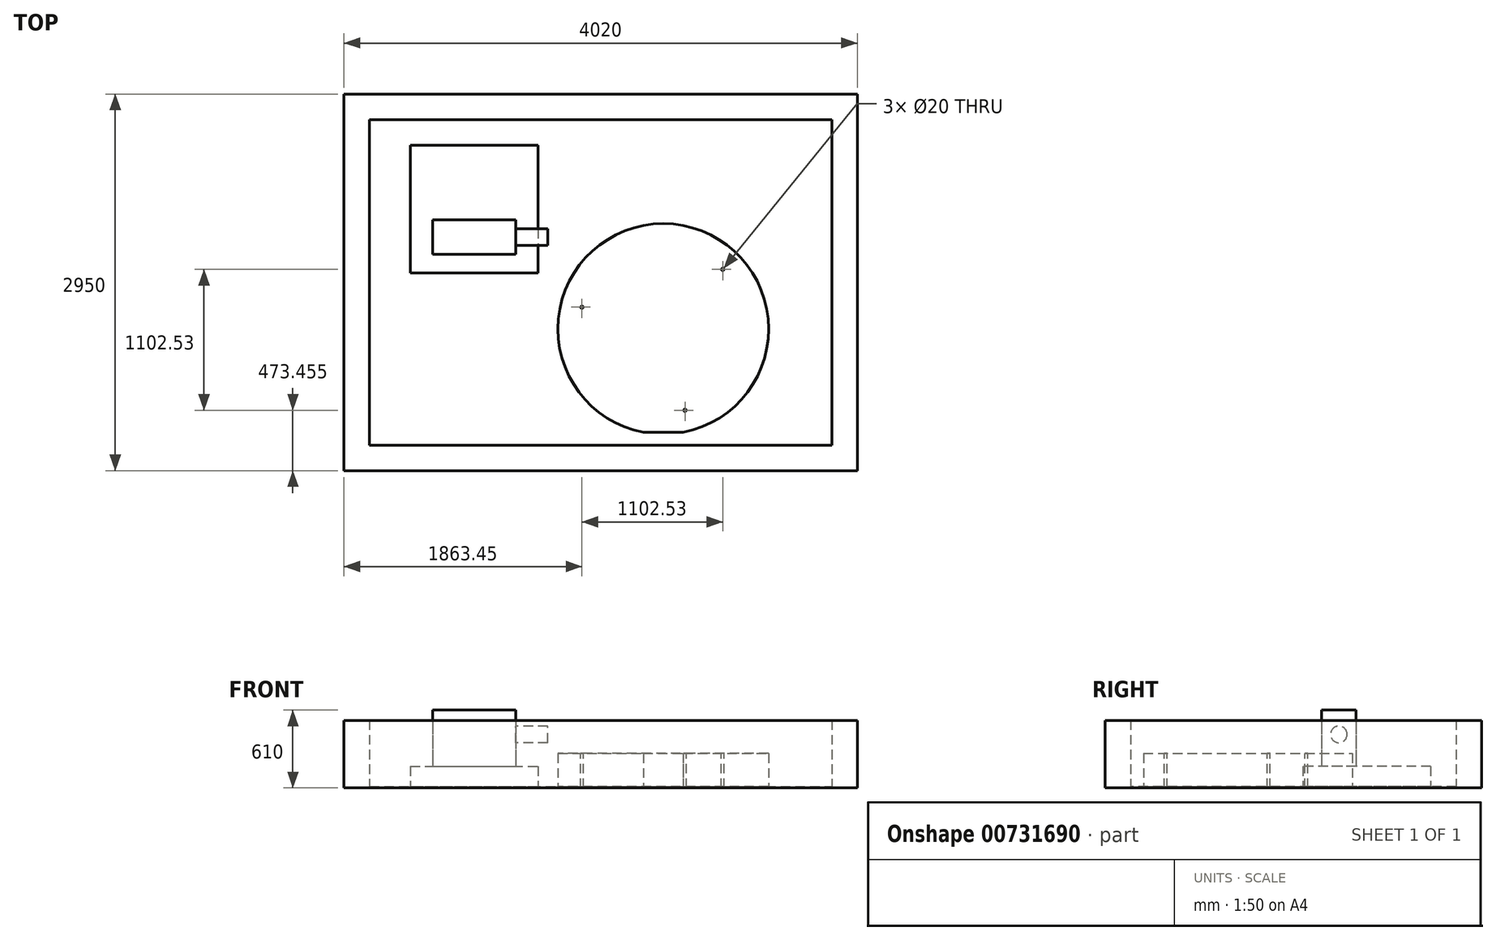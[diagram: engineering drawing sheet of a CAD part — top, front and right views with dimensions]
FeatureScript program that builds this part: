
annotation { "Feature Type Name" : "Feature", "Feature Type Description" : "" }
export const myFeature = defineFeature(function(context is Context, id is Id, definition is map)
    precondition{}
    {
        {
            var Q0;
            Q0=qCreatedBy(makeId("Top.planeOp"),FACE);
            var sketch = newSketch(context, id + "F0", { "sketchPlane" : qUnion([Q0])});
            skLineSegment(sketch, "E0.bottom", {"start": v(-2010, 1475) * mm, "end": v(2010, 1475) * mm});
            skLineSegment(sketch, "E0.top", {"start": v(-2010, -1475) * mm, "end": v(2010, -1475) * mm});
            skLineSegment(sketch, "E0.left", {"start": v(-2010, 1475) * mm, "end": v(-2010, -1475) * mm});
            skLineSegment(sketch, "E0.right", {"start": v(2010, 1475) * mm, "end": v(2010, -1475) * mm});
            skLineSegment(sketch, "E1", {"start": v(-2010, 1475) * mm, "end": v(2010, -1475) * mm, "construction": true});
            skSolve(sketch);
        }
        {
            var Q0;
            Q0=makeQuery(id+"F0.imprint","IMPRINT",FACE,{"disambiguationData":[TD([[makeQuery(id+"F0.imprint","IMPRINT",EDGE,{"derivedFrom":sQuery(id+"F0.wireOp",EDGE,"E0.bottom")}),-1.0]])]});
            extrude(context, id + "F1", {"entities" : qUnion([Q0]), "depth" : 10 * mm, "offsetDistance" : 25 * mm});
        }
        {
            var Q0;
            Q0=makeQuery(id+"F1.opExtrude","CAP_FACE",FACE,{"disambiguationData":[OSD([sQuery(id+"F0.wireOp",EDGE,"E0.bottom"),sQuery(id+"F0.wireOp",EDGE,"E0.top"),sQuery(id+"F0.wireOp",EDGE,"E0.left"),sQuery(id+"F0.wireOp",EDGE,"E0.right")])],"isStart":false});
            var sketch = newSketch(context, id + "F2", { "sketchPlane" : qUnion([Q0])});
            skLineSegment(sketch, "E2.bottom", {"start": v(-2010, 1475) * mm, "end": v(2010, 1475) * mm});
            skLineSegment(sketch, "E2.top", {"start": v(-2010, -1475) * mm, "end": v(2010, -1475) * mm});
            skLineSegment(sketch, "E2.left", {"start": v(-2010, 1475) * mm, "end": v(-2010, -1475) * mm});
            skLineSegment(sketch, "E2.right", {"start": v(2010, 1475) * mm, "end": v(2010, -1475) * mm});
            skLineSegment(sketch, "E3.bottom", {"start": v(-1810, 1275) * mm, "end": v(1810, 1275) * mm});
            skLineSegment(sketch, "E3.top", {"start": v(-1810, -1275) * mm, "end": v(1810, -1275) * mm});
            skLineSegment(sketch, "E3.left", {"start": v(-1810, 1275) * mm, "end": v(-1810, -1275) * mm});
            skLineSegment(sketch, "E3.right", {"start": v(1810, 1275) * mm, "end": v(1810, -1275) * mm});
            skSolve(sketch);
        }
        {
            var Q0;
            Q0 = qSketchRegion(id + "F2", true);
            extrude(context, id + "F3", {"entities" : qUnion([Q0]), "operationType" : NewBodyOperationType.ADD, "depth" : 520 * mm, "offsetDistance" : 25 * mm});
        }
        {
            var Q0;
            Q0=makeQuery(id+"F1.opExtrude","CAP_FACE",FACE,{"disambiguationData":[OSD([sQuery(id+"F0.wireOp",EDGE,"E0.bottom"),sQuery(id+"F0.wireOp",EDGE,"E0.top"),sQuery(id+"F0.wireOp",EDGE,"E0.left"),sQuery(id+"F0.wireOp",EDGE,"E0.right")])],"isStart":false});
            var sketch = newSketch(context, id + "F4", { "sketchPlane" : qUnion([Q0])});
            skLineSegment(sketch, "E4.bottom", {"start": v(-1490, 1075) * mm, "end": v(-490, 1075) * mm});
            skLineSegment(sketch, "E4.top", {"start": v(-1490, 75) * mm, "end": v(-490, 75) * mm});
            skLineSegment(sketch, "E4.left", {"start": v(-1490, 1075) * mm, "end": v(-1490, 75) * mm});
            skLineSegment(sketch, "E4.right", {"start": v(-490, 1075) * mm, "end": v(-490, 75) * mm});
            skSolve(sketch);
        }
        {
            var Q0;
            Q0 = qSketchRegion(id + "F4", true);
            extrude(context, id + "F5", {"entities" : qUnion([Q0]), "operationType" : NewBodyOperationType.ADD, "depth" : 160 * mm, "offsetDistance" : 25 * mm});
        }
        {
            var Q0;
            Q0=makeQuery(id+"F1.opExtrude","CAP_FACE",FACE,{"disambiguationData":[OSD([sQuery(id+"F0.wireOp",EDGE,"E0.bottom"),sQuery(id+"F0.wireOp",EDGE,"E0.top"),sQuery(id+"F0.wireOp",EDGE,"E0.left"),sQuery(id+"F0.wireOp",EDGE,"E0.right")])],"isStart":false});
            var sketch = newSketch(context, id + "F6", { "sketchPlane" : qUnion([Q0])});
            skArc(sketch, "E5", {"start": v(646.6, -1175) * mm, "mid": v(490, 460) * mm, "end": v(333.4, -1175) * mm});
            skLineSegment(sketch, "E6", {"start": v(333.4, -1175) * mm, "end": v(646.6, -1175) * mm});
            skCircle(sketch, "E7", {"center": v(490, -365) * mm, "radius": 659 * mm, "construction": true});
            skPoint(sketch, "E8", {"position": v(490, -1024) * mm});
            skLineSegment(sketch, "E9", {"start": v(490, -365) * mm, "end": v(660.56, -1001.55) * mm, "construction": true});
            skLineSegment(sketch, "E10", {"start": v(490, -365) * mm, "end": v(-146.55, -535.56) * mm, "construction": true});
            skLineSegment(sketch, "E11", {"start": v(490, -365) * mm, "end": v(955.98, 100.98) * mm, "construction": true});
            skSolve(sketch);
        }
        {
            var Q0;
            Q0 = qSketchRegion(id + "F6", true);
            extrude(context, id + "F7", {"entities" : qUnion([Q0]), "operationType" : NewBodyOperationType.ADD, "depth" : 260 * mm, "offsetDistance" : 25 * mm});
        }
        {
            var Q0;
            Q0=makeQuery(id+"F5.opExtrude","CAP_FACE",FACE,{"disambiguationData":[OSD([sQuery(id+"F4.wireOp",EDGE,"E4.bottom"),sQuery(id+"F4.wireOp",EDGE,"E4.top"),sQuery(id+"F4.wireOp",EDGE,"E4.left"),sQuery(id+"F4.wireOp",EDGE,"E4.right")])],"isStart":false});
            var sketch = newSketch(context, id + "F8", { "sketchPlane" : qUnion([Q0])});
            skLineSegment(sketch, "E12.bottom", {"start": v(-1315, 490) * mm, "end": v(-665, 490) * mm});
            skLineSegment(sketch, "E12.top", {"start": v(-1315, 220) * mm, "end": v(-665, 220) * mm});
            skLineSegment(sketch, "E12.left", {"start": v(-1315, 490) * mm, "end": v(-1315, 220) * mm});
            skLineSegment(sketch, "E12.right", {"start": v(-665, 490) * mm, "end": v(-665, 220) * mm});
            skLineSegment(sketch, "E13", {"start": v(-1315, 490) * mm, "end": v(-665, 220) * mm, "construction": true});
            skPoint(sketch, "E14", {"position": v(-990, 355) * mm});
            skSolve(sketch);
        }
        {
            var Q0;
            Q0 = qSketchRegion(id + "F8", true);
            extrude(context, id + "F9", {"entities" : qUnion([Q0]), "operationType" : NewBodyOperationType.ADD, "depth" : 440 * mm, "offsetDistance" : 25 * mm});
        }
        {
            var Q0;
            Q0=makeQuery(id+"F9.opExtrude","SWEPT_FACE",FACE,{"disambiguationData":[OSD([sQuery(id+"F8.wireOp",EDGE,"E12.right")])]});
            var sketch = newSketch(context, id + "F10", { "sketchPlane" : qUnion([Q0])});
            skCircle(sketch, "E15", {"center": v(355, 420) * mm, "radius": 65 * mm});
            skPoint(sketch, "E15.centerSnap0", {"position": v(355, 170) * mm});
            skSolve(sketch);
        }
        {
            var Q0;
            Q0 = qSketchRegion(id + "F10", true);
            extrude(context, id + "F11", {"entities" : qUnion([Q0]), "operationType" : NewBodyOperationType.ADD, "depth" : 250 * mm, "offsetDistance" : 25 * mm});
        }
        {
            var Q0;
            Q0=makeQuery(id+"F7.opExtrude","CAP_FACE",FACE,{"disambiguationData":[OSD([sQuery(id+"F6.wireOp",EDGE,"E5"),sQuery(id+"F6.wireOp",EDGE,"E6")])],"isStart":false});
            var sketch = newSketch(context, id + "F12", { "sketchPlane" : qUnion([Q0])});
            skCircle(sketch, "E16", {"center": v(490, -365) * mm, "radius": 659 * mm, "construction": true});
            skCircle(sketch, "E17", {"center": v(955.98, 100.98) * mm, "radius": 10 * mm});
            skCircle(sketch, "E18", {"center": v(660.56, -1001.55) * mm, "radius": 10 * mm});
            skCircle(sketch, "E19", {"center": v(-146.55, -194.44) * mm, "radius": 10 * mm});
            skLineSegment(sketch, "E20", {"start": v(490, -365) * mm, "end": v(-146.55, -194.44) * mm, "construction": true});
            skLineSegment(sketch, "E21", {"start": v(490, -365) * mm, "end": v(955.98, 100.98) * mm, "construction": true});
            skLineSegment(sketch, "E22", {"start": v(490, -365) * mm, "end": v(660.56, -1001.55) * mm, "construction": true});
            skLineSegment(sketch, "E23", {"start": v(490, 294) * mm, "end": v(490, -1024) * mm, "construction": true});
            skSolve(sketch);
        }
        {
            var Q0;
            Q0 = qSketchRegion(id + "F12", true);
            extrude(context, id + "F13", {"entities" : qUnion([Q0]), "operationType" : NewBodyOperationType.REMOVE, "oppositeDirection" : true, "depth" : 280 * mm, "offsetDistance" : 25 * mm});
        }
    });
